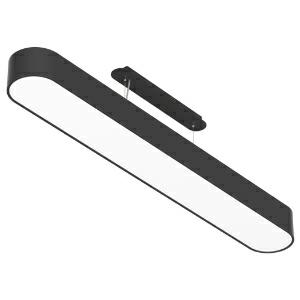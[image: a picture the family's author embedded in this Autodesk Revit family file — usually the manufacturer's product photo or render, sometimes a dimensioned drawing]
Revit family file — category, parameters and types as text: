
# Revit family: smoothline_1530x200_hl_led_48w_3840lm_3000k_cri80_410-1470
name_source: partatom
category: Leuchten
revit_build: Autodesk Revit 2016 (Build: 20190508_0715(x64)
units: mm (PartAtom-declared; Revit-internal decimal feet)

## family parameters
Basisbauteil = Fläche
Beim Laden mit Abzugskörper schneiden = Nein
Bemaßung runder Anschluss = Durchmesser verwenden
Gemeinsam genutzt = Nein
Lichtquelle = Nein
Raumberechnungspunkt = Nein
Teiletyp = Normal

## types (1)
- 410-1470-D01 (15 x LED, 429 lm, 3.2 W, 3000K)
    Approval mark = CE
    Beschreibung = The pendant luminaire SMOOTHLINE from the familiy SMOOTHY consists of aluminum-extruded profile. Charming SOFT-EDGE design ensure unparalleled styling. The ballast is integrated and allows for an operation with 220-240V (50/60Hz). SMOOTHLINE (# 410-1470) ist not dimmable (on/off). The luminaire with direct illumination and corresponds to protection class SK1 at IP20.
    CIE Flux Codes = 47 78 95 100 57
    Color Rendering = 1B/80…89
    Color Temperature = 3000K
    Height = 120 mm
    Hersteller = Prolicht
    Lamp Light Flux = 429 lm
    Lamp Power = 3.2 W
    Lamp count = 15
    Lampe = 15 x LED
    Length = 1530 mm
    Luminous efficacy = 76 lm/W
    ModVariant = Nein
    Modell = 410-1470
    Mounting Place = Ceiling
    Mounting Type = Pendant
    Number of Poles = 1
    OnlyDefault = Ja
    Power Factor = 1
    Product Name = SMOOTHLINE 1530x200 HL LED 48W 3840lm 3000K CRI80
    Product group = Suspended lights
    ProductGroupID = 941
    Protection Class = Protection class I
    Protection Degree = IP 20
    RLX_Detail_Level = 1
    RlxData = <blob elided: 35025 chars, md5=da7e8d8f>
    Scheinlast = 48 VA
    Socket = socket
    Standby Power = 0 W
    System Light Flux = 3652 lm
    System Power = 48 W
    Typenbild = 410-1470.jpg
    URL = http://relux.com
    VarID = 410-1470-d01
    Voltage = 0 V
    Vorgabe-Ansicht = 1800 mm
    Weight = 0.00 kg
    Width = 200 mm  [stored 0.656168 ft]

note: [stored X ft] marks values corroborated as IEEE doubles in the binary element streams (Revit-internal decimal feet)

## geometry (parser evidence)
native form markers: Sweep x10
no freeform markers — native parametric forms only
